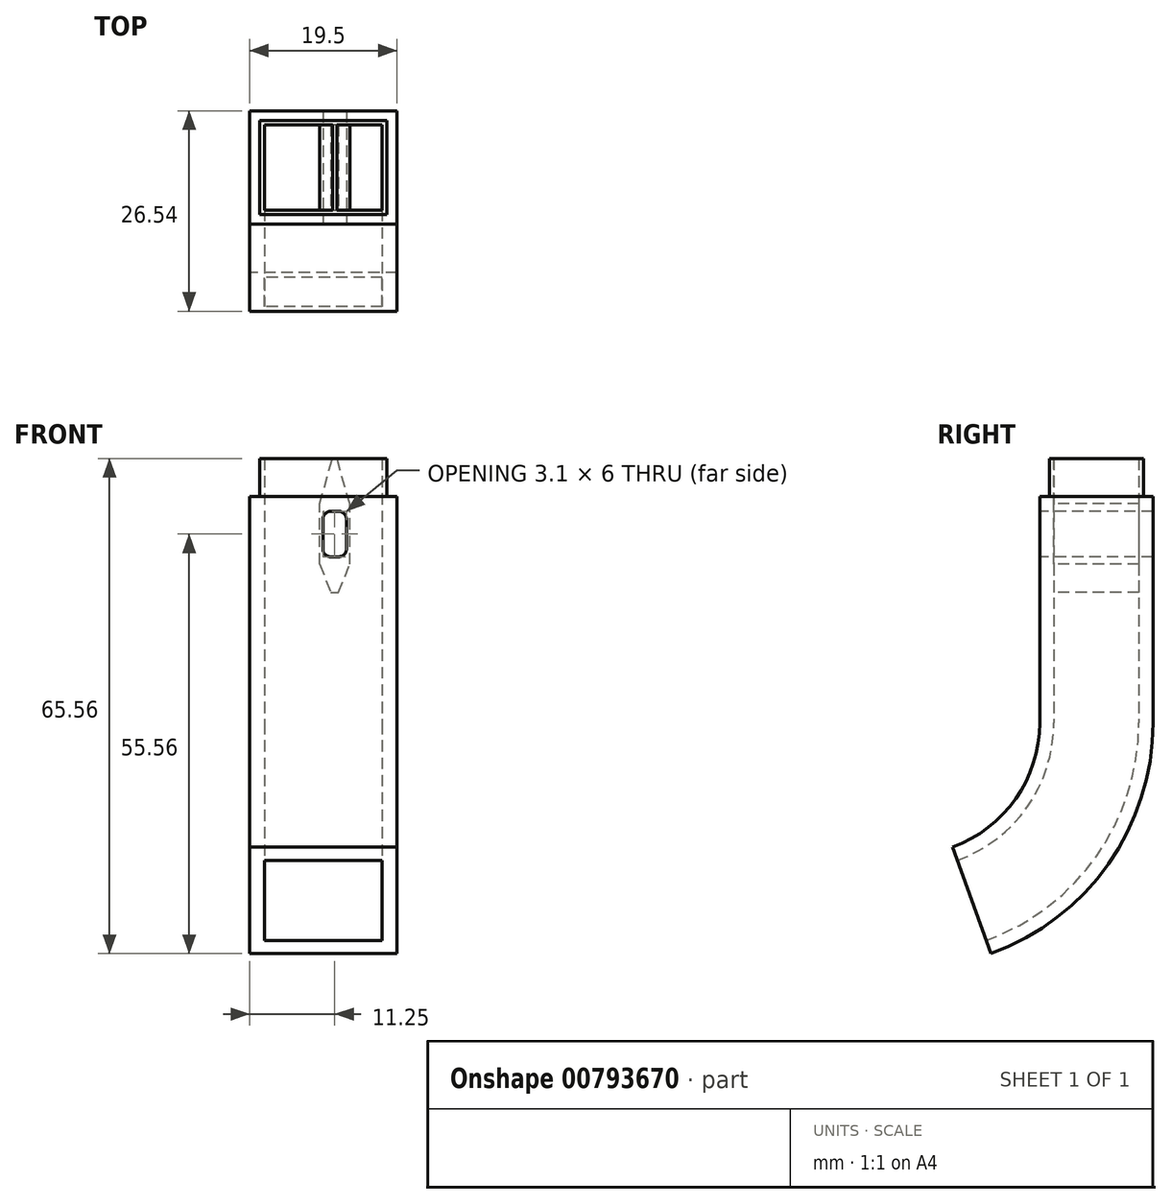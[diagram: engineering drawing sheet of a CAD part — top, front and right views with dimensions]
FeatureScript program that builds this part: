
annotation { "Feature Type Name" : "Feature", "Feature Type Description" : "" }
export const myFeature = defineFeature(function(context is Context, id is Id, definition is map)
    precondition{}
    {
        {
            var Q0;
            Q0=qCreatedBy(makeId("Top.planeOp"),FACE);
            var sketch = newSketch(context, id + "F0", { "sketchPlane" : qUnion([Q0])});
            skLineSegment(sketch, "E0.bottom", {"start": v(9.75, -7.5) * mm, "end": v(-9.75, -7.5) * mm});
            skLineSegment(sketch, "E0.top", {"start": v(9.75, 7.5) * mm, "end": v(-9.75, 7.5) * mm});
            skLineSegment(sketch, "E0.left", {"start": v(9.75, -7.5) * mm, "end": v(9.75, 7.5) * mm});
            skLineSegment(sketch, "E0.right", {"start": v(-9.75, -7.5) * mm, "end": v(-9.75, 7.5) * mm});
            skPoint(sketch, "E0.middle", {"position": v(0, 0) * mm});
            skSolve(sketch);
        }
        {
            var Q0;
            Q0=qCreatedBy(makeId("Right.planeOp"),FACE);
            var sketch = newSketch(context, id + "F1", { "sketchPlane" : qUnion([Q0])});
            skLineSegment(sketch, "E1", {"start": v(0, 0) * mm, "end": v(0, -35) * mm});
            skArc(sketch, "E2.filletArc", {"start": v(-16.48, -58.5) * mm, "mid": v(-4.53, -49.35) * mm, "end": v(0, -35) * mm});
            skLineSegment(sketch, "E3", {"start": v(-16.48, -58.5) * mm, "end": v(-77.6, -80.65) * mm});
            skSolve(sketch);
        }
        {
            var Q0;
            Q0=makeQuery(id+"F0.imprint","IMPRINT",FACE,{"disambiguationData":[TD([[makeQuery(id+"F0.imprint","IMPRINT",EDGE,{"derivedFrom":sQuery(id+"F0.wireOp",EDGE,"E0.bottom")}),-1.0]])]});
            var Q1;
            Q1=sQuery(id+"F1.wireOp",EDGE,"E1");
            var Q2;
            Q2=sQuery(id+"F1.wireOp",EDGE,"E2.filletArc");
            var Q3;
            Q3=sQuery(id+"F1.wireOp",EDGE,"YaOYuksl-nYBC-noCd-C8et-3nYt0wg2bsbM");
            var Q4;
            Q4=sQuery(id+"F1.wireOp",EDGE,"ca187eba-1296-4b61-9f2e-ad1c607dc70c.filletArc");
            var Q5;
            Q5=sQuery(id+"F1.wireOp",EDGE,"aHfBEX4p-85ZQ-rHio-i0Hn-GCyXMtXvmG3X");
            sweep(context, id + "F2", {"profiles" : qUnion([Q0]), "path" : qUnion([Q1, Q2, Q3, Q4, Q5])});
        }
        {
            var Q0;
            Q0=makeQuery(id+"F0.imprint","IMPRINT",FACE,{"disambiguationData":[TD([[makeQuery(id+"F0.imprint","IMPRINT",EDGE,{"derivedFrom":sQuery(id+"F0.wireOp",EDGE,"E0.bottom")}),-1.0]])]});
            var sketch = newSketch(context, id + "F3", { "sketchPlane" : qUnion([Q0])});
            skLineSegment(sketch, "E4.bottom", {"start": v(7.8, -5.62) * mm, "end": v(-7.8, -5.63) * mm});
            skLineSegment(sketch, "E4.top", {"start": v(7.8, 5.63) * mm, "end": v(-7.8, 5.62) * mm});
            skLineSegment(sketch, "E4.left", {"start": v(7.8, -5.62) * mm, "end": v(7.8, 5.63) * mm});
            skLineSegment(sketch, "E4.right", {"start": v(-7.8, -5.63) * mm, "end": v(-7.8, 5.62) * mm});
            skPoint(sketch, "E4.middle", {"position": v(0, 0) * mm});
            skSolve(sketch);
        }
        {
            var Q0;
            Q0=makeQuery(id+"F3.imprint","IMPRINT",FACE,{"disambiguationData":[TD([[makeQuery(id+"F3.imprint","IMPRINT",EDGE,{"derivedFrom":sQuery(id+"F3.wireOp",EDGE,"E4.bottom")}),-1.0]])]});
            var Q1;
            Q1=sQuery(id+"F1.wireOp",EDGE,"E1");
            var Q2;
            Q2=sQuery(id+"F1.wireOp",EDGE,"E2.filletArc");
            var Q3;
            Q3=sQuery(id+"F1.wireOp",EDGE,"YaOYuksl-nYBC-noCd-C8et-3nYt0wg2bsbM");
            var Q4;
            Q4=sQuery(id+"F1.wireOp",EDGE,"ca187eba-1296-4b61-9f2e-ad1c607dc70c.filletArc");
            var Q5;
            Q5=sQuery(id+"F1.wireOp",EDGE,"aHfBEX4p-85ZQ-rHio-i0Hn-GCyXMtXvmG3X");
            sweep(context, id + "F4", {"operationType" : NewBodyOperationType.REMOVE, "profiles" : qUnion([Q0]), "path" : qUnion([Q1, Q2, Q3, Q4, Q5])});
        }
        {
            var Q0;
            Q0=makeQuery(id+"F0.imprint","IMPRINT",FACE,{"disambiguationData":[TD([[makeQuery(id+"F0.imprint","IMPRINT",EDGE,{"derivedFrom":sQuery(id+"F0.wireOp",EDGE,"E0.bottom")}),-1.0]])]});
            var sketch = newSketch(context, id + "F5", { "sketchPlane" : qUnion([Q0])});
            skLineSegment(sketch, "E5.bottom", {"start": v(8.4, -6.22) * mm, "end": v(-8.4, -6.23) * mm});
            skLineSegment(sketch, "E5.top", {"start": v(8.4, 6.23) * mm, "end": v(-8.4, 6.22) * mm});
            skLineSegment(sketch, "E5.left", {"start": v(8.4, -6.22) * mm, "end": v(8.4, 6.23) * mm});
            skLineSegment(sketch, "E5.right", {"start": v(-8.4, -6.23) * mm, "end": v(-8.4, 6.22) * mm});
            skPoint(sketch, "E5.middle", {"position": v(0, 0) * mm});
            skLineSegment(sketch, "E6.0", {"start": v(9.75, -7.5) * mm, "end": v(-9.75, -7.5) * mm});
            skLineSegment(sketch, "E6.1", {"start": v(9.75, -7.5) * mm, "end": v(9.75, 7.5) * mm});
            skLineSegment(sketch, "E6.2", {"start": v(9.75, 7.5) * mm, "end": v(-9.75, 7.5) * mm});
            skLineSegment(sketch, "E6.3", {"start": v(-9.75, -7.5) * mm, "end": v(-9.75, 7.5) * mm});
            skSolve(sketch);
        }
        {
            var Q0;
            Q0=makeQuery(id+"F2.opSweep","SWEPT_FACE",FACE,{"disambiguationData":[OSD([sQuery(id+"F0.wireOp",EDGE,"E0.bottom"),sQuery(id+"F1.wireOp",EDGE,"E1")])]});
            var sketch = newSketch(context, id + "F6", { "sketchPlane" : qUnion([Q0])});
            skLineSegment(sketch, "E7.bottom", {"start": v(3.5, -14) * mm, "end": v(-0.5, -14) * mm});
            skLineSegment(sketch, "E7.left", {"start": v(3.5, -14) * mm, "end": v(3.5, -6) * mm});
            skLineSegment(sketch, "E7.right", {"start": v(-0.5, -14) * mm, "end": v(-0.5, -6) * mm});
            skPoint(sketch, "E7.middle", {"position": v(1.5, -10) * mm});
            skLineSegment(sketch, "E8", {"start": v(-0.5, -6) * mm, "end": v(1.2, 0) * mm});
            skLineSegment(sketch, "E9", {"start": v(1.2, 0) * mm, "end": v(1.8, 0) * mm, "construction": true});
            skLineSegment(sketch, "E10", {"start": v(1.2, 0) * mm, "end": v(1.8, 0) * mm});
            skLineSegment(sketch, "E11", {"start": v(3.5, -6) * mm, "end": v(1.8, 0) * mm});
            skLineSegment(sketch, "E12", {"start": v(1.5, 0) * mm, "end": v(1.5, -10) * mm, "construction": true});
            skLineSegment(sketch, "E13", {"start": v(-0.5, -14) * mm, "end": v(1, -17.74) * mm});
            skLineSegment(sketch, "E14", {"start": v(1, -17.74) * mm, "end": v(2, -17.74) * mm});
            skLineSegment(sketch, "E15", {"start": v(2, -17.74) * mm, "end": v(3.5, -14) * mm});
            skLineSegment(sketch, "E16", {"start": v(1.5, -10) * mm, "end": v(1.5, -17.74) * mm, "construction": true});
            skSolve(sketch);
        }
        {
            var Q0;
            Q0 = qSketchRegion(id + "F6", true);
            var Q1;
            Q1=makeQuery(id+"F2.opSweep","SWEPT_FACE",FACE,{"disambiguationData":[OSD([sQuery(id+"F0.wireOp",EDGE,"E0.top"),sQuery(id+"F1.wireOp",EDGE,"E1")])]});
            extrude(context, id + "F7", {"entities" : qUnion([Q0]), "operationType" : NewBodyOperationType.ADD, "endBound" : BoundingType.UP_TO_SURFACE, "oppositeDirection" : true, "depth" : 25 * mm, "endBoundEntityFace" : qUnion([Q1]), "offsetDistance" : 25 * mm});
        }
        {
            var Q0;
            Q0 = qSketchRegion(id + "F5", true);
            extrude(context, id + "F8", {"entities" : qUnion([Q0]), "operationType" : NewBodyOperationType.REMOVE, "oppositeDirection" : true, "depth" : 5 * mm, "offsetDistance" : 25 * mm});
        }
        {
            var Q0;
            Q0=makeQuery(id+"F2.opSweep","SWEPT_FACE",FACE,{"disambiguationData":[OSD([sQuery(id+"F0.wireOp",EDGE,"E0.bottom"),sQuery(id+"F1.wireOp",EDGE,"E1")])]});
            var sketch = newSketch(context, id + "F9", { "sketchPlane" : qUnion([Q0])});
            skLineSegment(sketch, "E17.bottom", {"start": v(3.05, -13) * mm, "end": v(-0.05, -13) * mm});
            skLineSegment(sketch, "E17.top", {"start": v(3.05, -7) * mm, "end": v(-0.05, -7) * mm});
            skLineSegment(sketch, "E17.left", {"start": v(3.05, -13) * mm, "end": v(3.05, -7) * mm});
            skLineSegment(sketch, "E17.right", {"start": v(-0.05, -13) * mm, "end": v(-0.05, -7) * mm});
            skPoint(sketch, "E17.middle", {"position": v(1.5, -10) * mm});
            skSolve(sketch);
        }
        {
            var Q0;
            Q0 = qSketchRegion(id + "F9", true);
            extrude(context, id + "F10", {"entities" : qUnion([Q0]), "operationType" : NewBodyOperationType.REMOVE, "endBound" : BoundingType.UP_TO_NEXT, "oppositeDirection" : true, "depth" : 25 * mm, "offsetDistance" : 25 * mm});
        }
        {
            var Q0;
            Q0=makeQuery(id+"F10.boolean.opBoolean","COPY",EDGE,{"derivedFrom":makeQuery(id+"F10.opExtrude","SWEPT_EDGE",EDGE,{"disambiguationData":[OSD([sQuery(id+"F9.wireOp",EDGE,"E17.top"),sQuery(id+"F9.wireOp",EDGE,"E17.right")])]})});
            var Q1;
            Q1=makeQuery(id+"F10.boolean.opBoolean","COPY",EDGE,{"derivedFrom":makeQuery(id+"F10.opExtrude","SWEPT_EDGE",EDGE,{"disambiguationData":[OSD([sQuery(id+"F9.wireOp",EDGE,"E17.top"),sQuery(id+"F9.wireOp",EDGE,"E17.left")])]})});
            var Q2;
            Q2=makeQuery(id+"F10.boolean.opBoolean","COPY",EDGE,{"derivedFrom":makeQuery(id+"F10.opExtrude","SWEPT_EDGE",EDGE,{"disambiguationData":[OSD([sQuery(id+"F9.wireOp",EDGE,"E17.bottom"),sQuery(id+"F9.wireOp",EDGE,"E17.right")])]})});
            var Q3;
            Q3=makeQuery(id+"F10.boolean.opBoolean","COPY",EDGE,{"derivedFrom":makeQuery(id+"F10.opExtrude","SWEPT_EDGE",EDGE,{"disambiguationData":[OSD([sQuery(id+"F9.wireOp",EDGE,"E17.bottom"),sQuery(id+"F9.wireOp",EDGE,"E17.left")])]})});
            fillet(context, id + "F11", {"entities" : qUnion([Q0, Q1, Q2, Q3]), "radius" : 1 * mm, "tangentPropagation" : true, "allowEdgeOverflow" : false});
        }
    });
